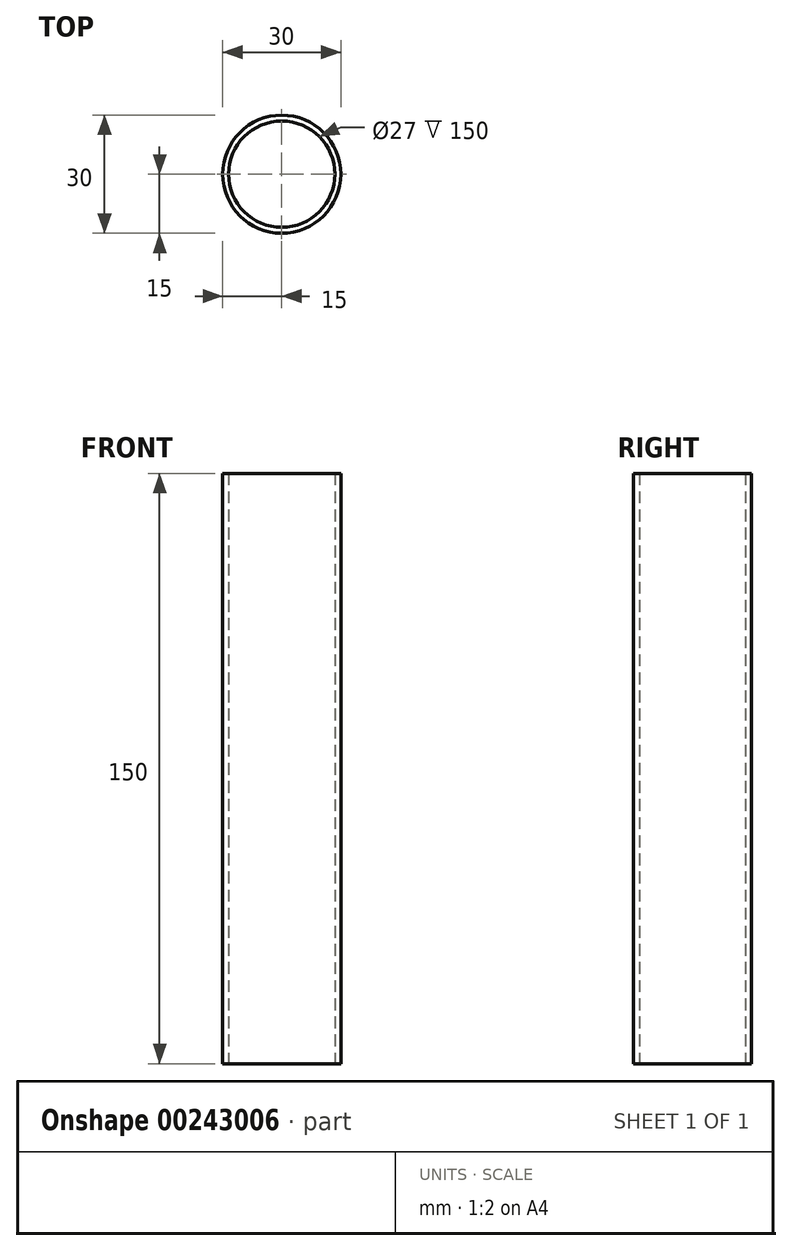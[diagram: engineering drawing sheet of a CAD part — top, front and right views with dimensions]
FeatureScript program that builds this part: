
annotation { "Feature Type Name" : "Feature", "Feature Type Description" : "" }
export const myFeature = defineFeature(function(context is Context, id is Id, definition is map)
    precondition{}
    {
        {
            var Q0;
            Q0=qCreatedBy(makeId("Top.planeOp"),FACE);
            var sketch = newSketch(context, id + "F0", { "sketchPlane" : qUnion([Q0])});
            skCircle(sketch, "E0", {"center": v(0, 0) * mm, "radius": 15 * mm});
            skCircle(sketch, "E1", {"center": v(0, 0) * mm, "radius": 13.5 * mm});
            skSolve(sketch);
        }
        {
            var Q0;
            Q0 = qSketchRegion(id + "F0", true);
            extrude(context, id + "F1", {"entities" : qUnion([Q0]), "depth" : 150 * mm});
        }
    });
